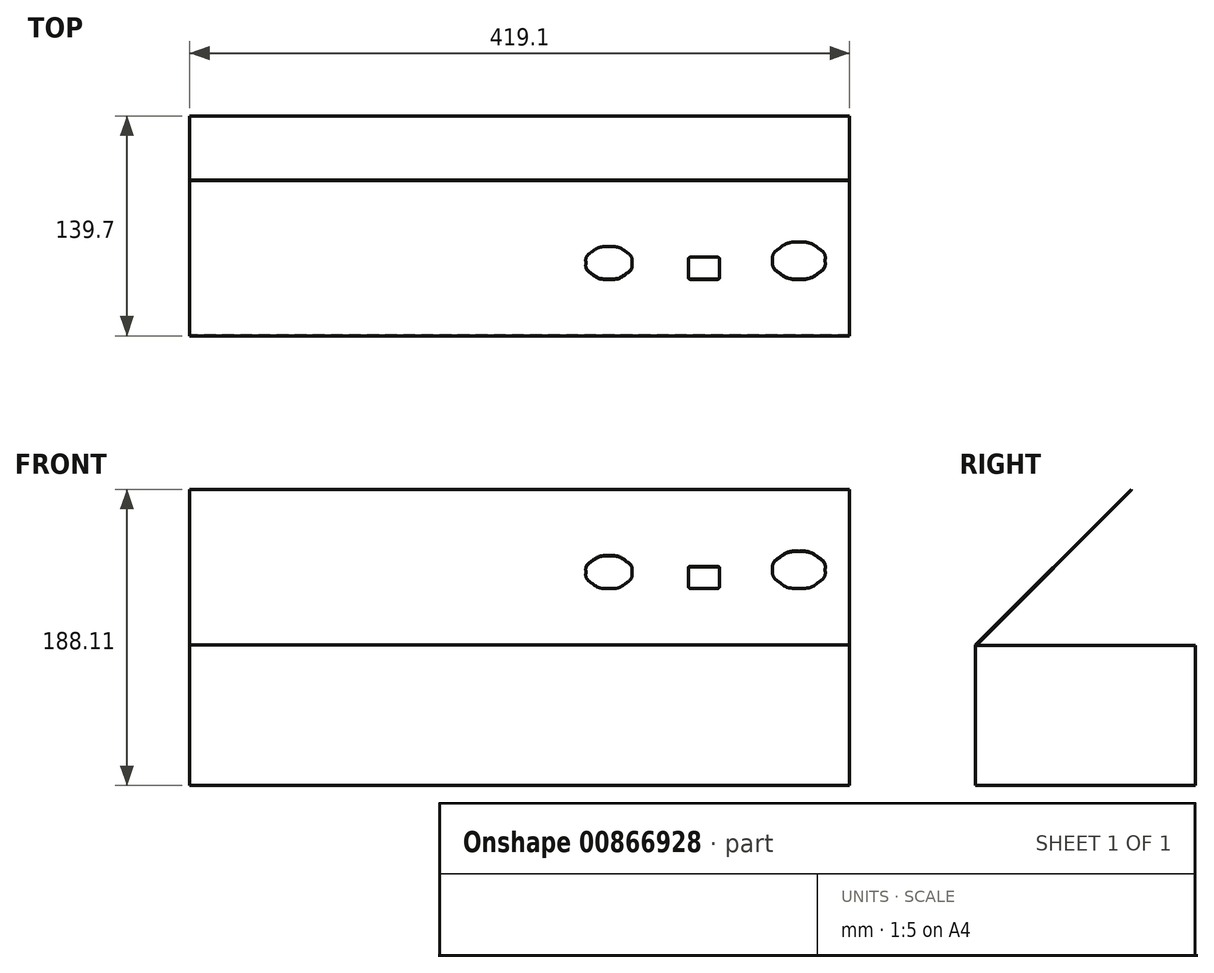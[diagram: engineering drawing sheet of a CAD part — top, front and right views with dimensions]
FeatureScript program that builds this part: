
annotation { "Feature Type Name" : "Feature", "Feature Type Description" : "" }
export const myFeature = defineFeature(function(context is Context, id is Id, definition is map)
    precondition{}
    {
        {
            var Q0;
            Q0=qCreatedBy(makeId("Right.planeOp"),FACE);
            var sketch = newSketch(context, id + "F0", { "sketchPlane" : qUnion([Q0])});
            skLineSegment(sketch, "E0.bottom", {"start": v(0, 0) * mm, "end": v(-139.7, 0) * mm});
            skLineSegment(sketch, "E0.top", {"start": v(0, 88.9) * mm, "end": v(-139.3, 88.9) * mm});
            skLineSegment(sketch, "E0.left", {"start": v(0, 0) * mm, "end": v(0, 88.9) * mm});
            skLineSegment(sketch, "E0.right", {"start": v(-139.7, 0) * mm, "end": v(-139.7, 89.32) * mm});
            skLineSegment(sketch, "E1", {"start": v(-139.7, 89.32) * mm, "end": v(-40.92, 188.1) * mm});
            skLineSegment(sketch, "E2", {"start": v(-40.92, 188.1) * mm, "end": v(-40.63, 187.82) * mm});
            skLineSegment(sketch, "E3", {"start": v(-40.63, 187.82) * mm, "end": v(-139.3, 89.15) * mm});
            skLineSegment(sketch, "E4", {"start": v(-139.3, 88.9) * mm, "end": v(-139.3, 89.15) * mm});
            skLineSegment(sketch, "E5", {"start": v(-139.3, 88.9) * mm, "end": v(-139.7, 88.9) * mm, "construction": true});
            skSolve(sketch);
        }
        {
            var Q0;
            Q0=qSketchRegion(id+"F0",true);
            extrude(context, id + "F1", {"entities" : qUnion([Q0]), "endBound" : BoundingType.SYMMETRIC, "depth" : 419.1 * mm, "offsetDistance" : 25.4 * mm});
        }
        {
            var Q0;
            Q0=makeQuery(id+"F1.opExtrude","SWEPT_FACE",FACE,{"disambiguationData":[OSD([sQuery(id+"F0.wireOp",EDGE,"E1")])]});
            var sketch = newSketch(context, id + "F2", { "sketchPlane" : qUnion([Q0])});
            skLineSegment(sketch, "E6", {"start": v(107.06, 33.44) * mm, "end": v(107.06, 16.77) * mm});
            skLineSegment(sketch, "E7", {"start": v(126.9, 16.77) * mm, "end": v(126.9, 33.44) * mm});
            skLineSegment(sketch, "E8", {"start": v(-210.05, -35.62) * mm, "end": v(-210.05, 103.29) * mm, "construction": true});
            skLineSegment(sketch, "E9", {"start": v(209.05, -35.62) * mm, "end": v(209.05, 103.29) * mm, "construction": true});
            skLineSegment(sketch, "E10", {"start": v(-210.05, 103.29) * mm, "end": v(209.05, 103.29) * mm, "construction": true});
            skLineSegment(sketch, "E11", {"start": v(108.64, 15.18) * mm, "end": v(125.31, 15.18) * mm});
            skLineSegment(sketch, "E12", {"start": v(125.31, 35.02) * mm, "end": v(108.64, 35.02) * mm});
            skLineSegment(sketch, "E13", {"start": v(209.05, -35.62) * mm, "end": v(-210.05, -35.62) * mm, "construction": true});
            skFitSpline(sketch, "E14", {"points": [v(56.65, 44.55) * mm, v(52.8, 44.55) * mm, v(48.99, 42.97) * mm, v(46.27, 40.25) * mm]});
            skFitSpline(sketch, "E15", {"points": [v(46.27, 40.25) * mm, v(43.55, 37.53) * mm, v(41.97, 33.71) * mm, v(41.97, 29.87) * mm, v(41.97, 26.02) * mm, v(43.55, 22.2) * mm, v(46.27, 19.48) * mm]});
            skFitSpline(sketch, "E16", {"points": [v(46.27, 19.48) * mm, v(48.99, 16.76) * mm, v(52.8, 15.18) * mm, v(56.65, 15.18) * mm, v(60.5, 15.18) * mm, v(64.32, 16.76) * mm, v(67.04, 19.48) * mm]});
            skFitSpline(sketch, "E17", {"points": [v(67.04, 19.48) * mm, v(69.76, 22.2) * mm, v(71.34, 26.02) * mm, v(71.34, 29.87) * mm, v(71.34, 33.71) * mm, v(69.76, 37.53) * mm, v(67.04, 40.25) * mm]});
            skFitSpline(sketch, "E18", {"points": [v(67.04, 40.25) * mm, v(64.32, 42.97) * mm, v(60.5, 44.55) * mm, v(56.65, 44.55) * mm]});
            skFitSpline(sketch, "E19", {"points": [v(108.64, 35.02) * mm, v(108.23, 35.02) * mm, v(107.81, 34.85) * mm, v(107.52, 34.56) * mm]});
            skFitSpline(sketch, "E20", {"points": [v(107.52, 34.56) * mm, v(107.23, 34.27) * mm, v(107.06, 33.85) * mm, v(107.06, 33.44) * mm]});
            skFitSpline(sketch, "E21", {"points": [v(107.06, 16.77) * mm, v(107.06, 16.35) * mm, v(107.23, 15.94) * mm, v(107.52, 15.65) * mm]});
            skFitSpline(sketch, "E22", {"points": [v(107.52, 15.65) * mm, v(107.81, 15.35) * mm, v(108.23, 15.18) * mm, v(108.64, 15.18) * mm]});
            skFitSpline(sketch, "E23", {"points": [v(125.31, 15.18) * mm, v(125.73, 15.18) * mm, v(126.14, 15.35) * mm, v(126.44, 15.65) * mm]});
            skFitSpline(sketch, "E24", {"points": [v(126.44, 15.65) * mm, v(126.73, 15.94) * mm, v(126.9, 16.35) * mm, v(126.9, 16.77) * mm]});
            skFitSpline(sketch, "E25", {"points": [v(126.9, 33.44) * mm, v(126.9, 33.85) * mm, v(126.73, 34.27) * mm, v(126.44, 34.56) * mm]});
            skFitSpline(sketch, "E26", {"points": [v(126.44, 34.56) * mm, v(126.14, 34.85) * mm, v(125.73, 35.02) * mm, v(125.31, 35.02) * mm]});
            skFitSpline(sketch, "E27", {"points": [v(177.3, 48.52) * mm, v(172.94, 48.52) * mm, v(168.6, 46.72) * mm, v(165.52, 43.64) * mm]});
            skFitSpline(sketch, "E28", {"points": [v(165.52, 43.64) * mm, v(162.43, 40.55) * mm, v(160.63, 36.21) * mm, v(160.63, 31.85) * mm, v(160.63, 27.49) * mm, v(162.43, 23.15) * mm, v(165.52, 20.06) * mm]});
            skFitSpline(sketch, "E29", {"points": [v(165.52, 20.06) * mm, v(168.6, 16.98) * mm, v(172.94, 15.18) * mm, v(177.3, 15.18) * mm, v(181.67, 15.18) * mm, v(186, 16.98) * mm, v(189.09, 20.06) * mm]});
            skFitSpline(sketch, "E30", {"points": [v(189.09, 20.06) * mm, v(192.18, 23.15) * mm, v(193.97, 27.49) * mm, v(193.97, 31.85) * mm, v(193.97, 36.21) * mm, v(192.18, 40.55) * mm, v(189.09, 43.64) * mm]});
            skFitSpline(sketch, "E31", {"points": [v(189.09, 43.64) * mm, v(186, 46.72) * mm, v(181.67, 48.52) * mm, v(177.3, 48.52) * mm]});
            skSolve(sketch);
        }
        {
            var Q0;
            Q0=qSketchRegion(id+"F2",true);
            var Q1;
            Q1=makeQuery(id+"F1.opExtrude","SWEPT_FACE",FACE,{"disambiguationData":[OSD([sQuery(id+"F0.wireOp",EDGE,"E3")])]});
            extrude(context, id + "F3", {"entities" : qUnion([Q0]), "operationType" : NewBodyOperationType.REMOVE, "endBound" : BoundingType.UP_TO_SURFACE, "oppositeDirection" : true, "depth" : 25.4 * mm, "endBoundEntityFace" : qUnion([Q1]), "offsetDistance" : 25.4 * mm});
        }
    });
